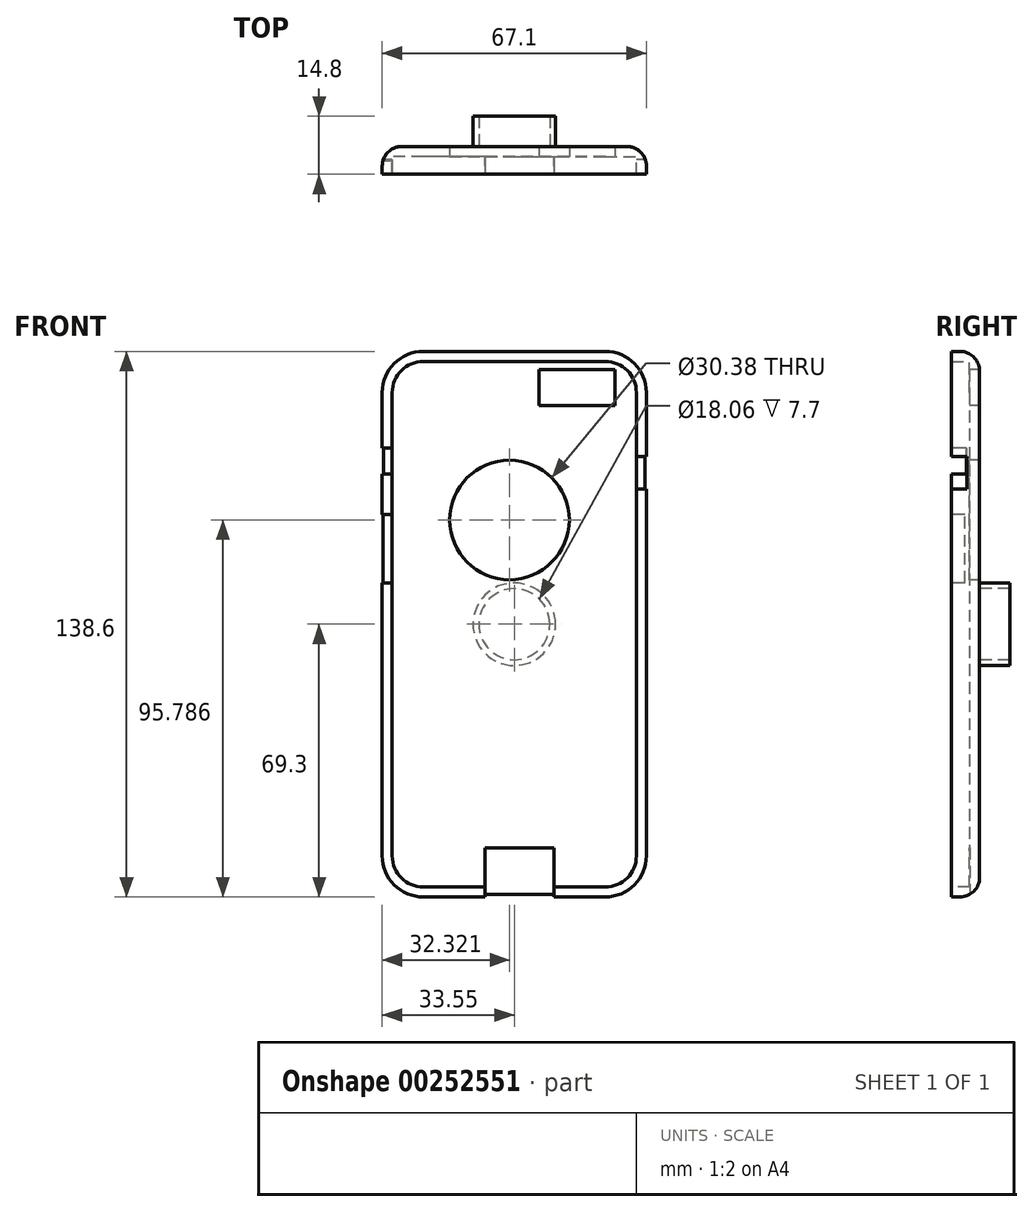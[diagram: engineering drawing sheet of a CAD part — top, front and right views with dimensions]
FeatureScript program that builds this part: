
annotation { "Feature Type Name" : "Feature", "Feature Type Description" : "" }
export const myFeature = defineFeature(function(context is Context, id is Id, definition is map)
    precondition{}
    {
        {
            var Q0;
            Q0=qCreatedBy(makeId("Front.planeOp"),FACE);
            var sketch = newSketch(context, id + "F0", { "sketchPlane" : qUnion([Q0])});
            skLineSegment(sketch, "E0.bottom", {"start": v(33.55, 69.3) * mm, "end": v(-33.55, 69.3) * mm});
            skLineSegment(sketch, "E0.top", {"start": v(33.55, -69.3) * mm, "end": v(-33.55, -69.3) * mm});
            skLineSegment(sketch, "E0.left", {"start": v(33.55, 69.3) * mm, "end": v(33.55, -69.3) * mm});
            skLineSegment(sketch, "E0.right", {"start": v(-33.55, 69.3) * mm, "end": v(-33.55, -69.3) * mm});
            skPoint(sketch, "E0.middle", {"position": v(0, 0) * mm});
            skSolve(sketch);
        }
        {
            var Q0;
            Q0 = qSketchRegion(id + "F0", true);
            extrude(context, id + "F1", {"entities" : qUnion([Q0]), "depth" : 7.1 * mm});
        }
        {
            var Q0;
            Q0=makeQuery(id+"F1.opExtrude","SWEPT_EDGE",EDGE,{"disambiguationData":[OSD([sQuery(id+"F0.wireOp",EDGE,"E0.bottom"),sQuery(id+"F0.wireOp",EDGE,"E0.left")])]});
            var Q1;
            Q1=makeQuery(id+"F1.opExtrude","SWEPT_EDGE",EDGE,{"disambiguationData":[OSD([sQuery(id+"F0.wireOp",EDGE,"E0.bottom"),sQuery(id+"F0.wireOp",EDGE,"E0.right")])]});
            var Q2;
            Q2=makeQuery(id+"F1.opExtrude","SWEPT_EDGE",EDGE,{"disambiguationData":[OSD([sQuery(id+"F0.wireOp",EDGE,"E0.top"),sQuery(id+"F0.wireOp",EDGE,"E0.right")])]});
            var Q3;
            Q3=makeQuery(id+"F1.opExtrude","SWEPT_EDGE",EDGE,{"disambiguationData":[OSD([sQuery(id+"F0.wireOp",EDGE,"E0.top"),sQuery(id+"F0.wireOp",EDGE,"E0.left")])]});
            fillet(context, id + "F2", {"entities" : qUnion([Q0, Q1, Q2, Q3]), "radius" : 10.42 * mm, "tangentPropagation" : true, "allowEdgeOverflow" : false});
        }
        {
            var Q0;
            Q0=makeQuery(id+"F1.opExtrude","CAP_FACE",FACE,{"disambiguationData":[OSD([sQuery(id+"F0.wireOp",EDGE,"E0.bottom"),sQuery(id+"F0.wireOp",EDGE,"E0.top"),sQuery(id+"F0.wireOp",EDGE,"E0.left"),sQuery(id+"F0.wireOp",EDGE,"E0.right")])],"isStart":false});
            shell(context, id + "F3", {"entities" : qUnion([Q0]), "thickness" : 2.54 * mm});
        }
        {
            var Q0;
            Q0=qCreatedBy(makeId("Front.planeOp"),FACE);
            var sketch = newSketch(context, id + "F4", { "sketchPlane" : qUnion([Q0])});
            skLineSegment(sketch, "E1.bottom", {"start": v(6.31, 64.7) * mm, "end": v(25.53, 64.7) * mm});
            skLineSegment(sketch, "E1.top", {"start": v(6.31, 55.51) * mm, "end": v(25.53, 55.51) * mm});
            skLineSegment(sketch, "E1.left", {"start": v(6.31, 64.7) * mm, "end": v(6.31, 55.51) * mm});
            skLineSegment(sketch, "E1.right", {"start": v(25.53, 64.7) * mm, "end": v(25.53, 55.51) * mm});
            skSolve(sketch);
        }
        {
            var Q0;
            Q0=makeQuery(id+"F4.imprint","IMPRINT",FACE,{"disambiguationData":[TD([[makeQuery(id+"F4.imprint","IMPRINT",EDGE,{"derivedFrom":sQuery(id+"F4.wireOp",EDGE,"E1.bottom")}),-1.0]])]});
            extrude(context, id + "F5", {"entities" : qUnion([Q0]), "operationType" : NewBodyOperationType.REMOVE, "endBound" : BoundingType.SYMMETRIC, "oppositeDirection" : true, "depth" : 25 * mm});
        }
        {
            var Q0;
            Q0=makeQuery(id+"F1.opExtrude","SWEPT_FACE",FACE,{"disambiguationData":[OSD([sQuery(id+"F0.wireOp",EDGE,"E0.top")])]});
            var sketch = newSketch(context, id + "F6", { "sketchPlane" : qUnion([Q0])});
            skLineSegment(sketch, "E2.bottom", {"start": v(-7.46, 2.44) * mm, "end": v(10.04, 2.44) * mm});
            skLineSegment(sketch, "E2.top", {"start": v(-7.46, 7.1) * mm, "end": v(10.04, 7.1) * mm});
            skLineSegment(sketch, "E2.left", {"start": v(-7.46, 2.44) * mm, "end": v(-7.46, 7.1) * mm});
            skLineSegment(sketch, "E2.right", {"start": v(10.04, 2.44) * mm, "end": v(10.04, 7.1) * mm});
            skSolve(sketch);
        }
        {
            var Q0;
            Q0=makeQuery(id+"F6.imprint","IMPRINT",FACE,{"disambiguationData":[TD([[makeQuery(id+"F6.imprint","IMPRINT",EDGE,{"derivedFrom":sQuery(id+"F6.wireOp",EDGE,"E2.bottom")}),1.0]])]});
            extrude(context, id + "F7", {"entities" : qUnion([Q0]), "operationType" : NewBodyOperationType.REMOVE, "endBound" : BoundingType.SYMMETRIC, "oppositeDirection" : true, "depth" : 25 * mm});
        }
        {
            var Q0;
            Q0=qCreatedBy(makeId("Front.planeOp"),FACE);
            var sketch = newSketch(context, id + "F8", { "sketchPlane" : qUnion([Q0])});
            skLineSegment(sketch, "E3.bottom", {"start": v(33.97, 43.82) * mm, "end": v(37.04, 43.82) * mm});
            skLineSegment(sketch, "E3.top", {"start": v(33.97, 29.68) * mm, "end": v(37.04, 29.68) * mm});
            skLineSegment(sketch, "E3.left", {"start": v(33.97, 43.82) * mm, "end": v(33.97, 29.68) * mm});
            skLineSegment(sketch, "E3.right", {"start": v(37.04, 43.82) * mm, "end": v(37.04, 29.68) * mm});
            skSolve(sketch);
        }
        {
            var Q0;
            Q0 = qSketchRegion(id + "F8", true);
            extrude(context, id + "F9", {"entities" : qUnion([Q0]), "operationType" : NewBodyOperationType.REMOVE, "endBound" : BoundingType.SYMMETRIC, "oppositeDirection" : true, "depth" : 25 * mm});
        }
        {
            var Q0;
            Q0=makeQuery(id+"F1.opExtrude","SWEPT_FACE",FACE,{"disambiguationData":[OSD([sQuery(id+"F0.wireOp",EDGE,"E0.right")])]});
            var sketch = newSketch(context, id + "F10", { "sketchPlane" : qUnion([Q0])});
            skLineSegment(sketch, "E4.bottom", {"start": v(7.1, 44.73) * mm, "end": v(3.38, 44.73) * mm});
            skLineSegment(sketch, "E4.top", {"start": v(7.1, 38.15) * mm, "end": v(3.38, 38.15) * mm});
            skLineSegment(sketch, "E4.left", {"start": v(7.1, 44.73) * mm, "end": v(7.1, 38.15) * mm});
            skLineSegment(sketch, "E4.right", {"start": v(3.38, 44.73) * mm, "end": v(3.38, 38.15) * mm});
            skSolve(sketch);
        }
        {
            var Q0;
            Q0=makeQuery(id+"F10.imprint","IMPRINT",FACE,{"disambiguationData":[TD([[makeQuery(id+"F10.imprint","IMPRINT",EDGE,{"derivedFrom":sQuery(id+"F10.wireOp",EDGE,"E4.bottom")}),1.0]])]});
            extrude(context, id + "F11", {"entities" : qUnion([Q0]), "operationType" : NewBodyOperationType.REMOVE, "endBound" : BoundingType.SYMMETRIC, "oppositeDirection" : true, "depth" : 25 * mm});
        }
        {
            var Q0;
            Q0=makeQuery(id+"F1.opExtrude","SWEPT_FACE",FACE,{"disambiguationData":[OSD([sQuery(id+"F0.wireOp",EDGE,"E0.right")])]});
            var sketch = newSketch(context, id + "F12", { "sketchPlane" : qUnion([Q0])});
            skLineSegment(sketch, "E5.bottom", {"start": v(7.1, 27.82) * mm, "end": v(3.76, 27.82) * mm});
            skLineSegment(sketch, "E5.top", {"start": v(7.1, 10.53) * mm, "end": v(3.76, 10.53) * mm});
            skLineSegment(sketch, "E5.left", {"start": v(7.1, 27.82) * mm, "end": v(7.1, 10.53) * mm});
            skLineSegment(sketch, "E5.right", {"start": v(3.76, 27.82) * mm, "end": v(3.76, 10.53) * mm});
            skSolve(sketch);
        }
        {
            var Q0;
            Q0=makeQuery(id+"F12.imprint","IMPRINT",FACE,{"disambiguationData":[TD([[makeQuery(id+"F12.imprint","IMPRINT",EDGE,{"derivedFrom":sQuery(id+"F12.wireOp",EDGE,"E5.bottom")}),1.0]])]});
            extrude(context, id + "F13", {"entities" : qUnion([Q0]), "operationType" : NewBodyOperationType.REMOVE, "endBound" : BoundingType.SYMMETRIC, "oppositeDirection" : true, "depth" : 25 * mm});
        }
        {
            var Q0;
            Q0=makeQuery(id+"F1.opExtrude","SWEPT_FACE",FACE,{"disambiguationData":[OSD([sQuery(id+"F0.wireOp",EDGE,"E0.left")])]});
            var sketch = newSketch(context, id + "F14", { "sketchPlane" : qUnion([Q0])});
            skLineSegment(sketch, "E6.bottom", {"start": v(-7.1, 42.66) * mm, "end": v(-3.2, 42.66) * mm});
            skLineSegment(sketch, "E6.top", {"start": v(-7.1, 34.4) * mm, "end": v(-3.2, 34.4) * mm});
            skLineSegment(sketch, "E6.left", {"start": v(-7.1, 42.66) * mm, "end": v(-7.1, 34.4) * mm});
            skLineSegment(sketch, "E6.right", {"start": v(-3.2, 42.66) * mm, "end": v(-3.2, 34.4) * mm});
            skSolve(sketch);
        }
        {
            var Q0;
            Q0=makeQuery(id+"F14.imprint","IMPRINT",FACE,{"disambiguationData":[TD([[makeQuery(id+"F14.imprint","IMPRINT",EDGE,{"derivedFrom":sQuery(id+"F14.wireOp",EDGE,"E6.bottom")}),-1.0]])]});
            extrude(context, id + "F15", {"entities" : qUnion([Q0]), "operationType" : NewBodyOperationType.REMOVE, "endBound" : BoundingType.SYMMETRIC, "oppositeDirection" : true, "depth" : 25 * mm});
        }
        {
            var Q0;
            Q0=makeQuery(id+"F1.opExtrude","CAP_EDGE",EDGE,{"disambiguationData":[OSD([sQuery(id+"F0.wireOp",EDGE,"E0.left")])],"isStart":true});
            fillet(context, id + "F16", {"entities" : qUnion([Q0]), "radius" : 5 * mm, "tangentPropagation" : true, "allowEdgeOverflow" : false});
        }
        {
            var Q0;
            Q0=qCreatedBy(makeId("Front.planeOp"),FACE);
            var sketch = newSketch(context, id + "F17", { "sketchPlane" : qUnion([Q0])});
            skCircle(sketch, "E7", {"center": v(-1.23, 26.49) * mm, "radius": 15.19 * mm});
            skPoint(sketch, "E7.first.point", {"position": v(8.32, 38.3) * mm});
            skPoint(sketch, "E7.second.point", {"position": v(-10.9, 14.77) * mm});
            skPoint(sketch, "E7.third.point", {"position": v(12.34, 19.65) * mm});
            skSolve(sketch);
        }
        {
            var Q0;
            Q0 = qSketchRegion(id + "F17", true);
            extrude(context, id + "F18", {"entities" : qUnion([Q0]), "operationType" : NewBodyOperationType.REMOVE, "endBound" : BoundingType.SYMMETRIC, "oppositeDirection" : true, "depth" : 25 * mm});
        }
        {
            var Q0;
            Q0=qCreatedBy(makeId("Front.planeOp"),FACE);
            var sketch = newSketch(context, id + "F19", { "sketchPlane" : qUnion([Q0])});
            skCircle(sketch, "E8", {"center": v(0, 0) * mm, "radius": 10.48 * mm});
            skCircle(sketch, "E9", {"center": v(0, 0) * mm, "radius": 9.03 * mm});
            skSolve(sketch);
        }
        {
            var Q0;
            Q0 = qSketchRegion(id + "F19", true);
            extrude(context, id + "F20", {"entities" : qUnion([Q0]), "operationType" : NewBodyOperationType.ADD, "oppositeDirection" : true, "depth" : 7.7 * mm});
        }
    });
